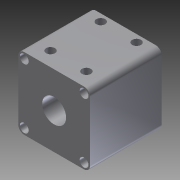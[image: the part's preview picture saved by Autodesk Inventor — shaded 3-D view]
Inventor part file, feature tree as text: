
AUTODESK INVENTOR PART (.ipt)
format: ipt  version: 2012 SP1 (Build 160190100, 190)  size: 140,800 bytes
history: native  units: in
note: dims shown in document units (in); Inventor stores cm internally (conversion verified against a paired STEP export)
features: extrude x3, sketch x3, fillet x1
ambient origin geometry x8: Origin, YZ Plane, XZ Plane, XY Plane, X Axis, Y Axis, Z Axis, Center Point
bodies: Solid1 (feature_tree)
feature tree (7):
  extrude  "Extrusion1"  Depth=1.5in
  fillet  "Fillet1"  Radius=0.5in
  extrude  "Extrusion2"  Depth=0.75in
  extrude  "Extrusion3"  Depth=0.125in
  sketch  "Sketch1"  dims[d0=1.5in d1=1.5in d2=0.5in]
  sketch  "Sketch2"  dims[d3=0.75in d4=0.75in]
  sketch  "Sketch3"  dims[d5=1.5in d6=0.0in d7=0.125in d8=0.185in d9=0.7874in d11=0.75in d12=0.7874in d14=1.05in d17=0.15in d18=0.375in d19=0.3in d20=0.0in d21=0.185in d22=0.7874in d24=0.75in d25=0.7874in d27=1.05in d30=0.15in d31=0.375in d32=0.3in d33=0.0in d34=0.185in d35=0.7874in d37=1.25in d38=0.7874in d40=1.25in d43=0.125in d44=0.125in]
